# Revit family: 306_acb0105b96fc40aca24c2fe25a676a
name_source: partatom
category: Pipe Accessories
units: mm (PartAtom-declared; Revit-internal decimal feet)

## family parameters
Always vertical = Yes
Cut with Voids When Loaded = No
Part Type = Valve - Breaks Into
Round Connector Dimension = Use Diameter
Shared = No
Work Plane-Based = No

## types (4) — shared parameters
Description = 2-way Motorized ball valve MBA122, PN32 external thread with adapters
H1 = 1 mm  [stored 0.00328084 ft]
L2D_Min = 3048 mm
Manufacturer = ESBE
QmdConnectorList = 301;D;302;D
URL = http://www.esbe.eu
X15 = 8 mm  [stored 0.0262467 ft]
X15__ve = -8 mm  [stored -0.0262467 ft]
X16 = 6 mm  [stored 0.019685 ft]
X16__ve = -6 mm  [stored -0.019685 ft]
X8 = 4 mm  [stored 0.0131234 ft]
Y0 = 5 mm  [stored 0.0164042 ft]
Y11 = 3 mm  [stored 0.00984252 ft]
Z3 = 11 mm
Z4 = 52 mm
Z6 = 35 mm
Z6__ve = -35 mm
Z7 = 3 mm  [stored 0.00984252 ft]
magiPartTypeId = 306
magiProductFamilyId = acb0105b96fc40aca24c2fe25a676a

## per-type parameters (varying)
- MBA122 G1  MM WA 230VAC 2-P 10NM: C=73 mm; CenSd_Y13_6=14 mm  [stored 0.0459318 ft]; D=25 mm; E=29 mm; L2D=133 mm; W2D=25 mm; X1=75 mm; X12=58 mm; X12__ve=-58 mm; X14=4 mm  [stored 0.0131234 ft]; X17=47 mm; X5=3 mm  [stored 0.00984252 ft]; X5__ve=-3 mm; X6=33 mm; X7=20 mm  [stored 0.0656168 ft]; X7__ve=-20 mm; Y1=13 mm  [stored 0.0426509 ft]; Y10=19 mm; Y10__ve=-19 mm; Y12=15 mm  [stored 0.0492126 ft]; Y13=16 mm  [stored 0.0524934 ft]; Y14=14 mm  [stored 0.0459318 ft]; Y2=13 mm  [stored 0.0426509 ft]; Y4=15 mm  [stored 0.0492126 ft]; Y5=16 mm  [stored 0.0524934 ft]; Z2=26 mm; Z2__ve=-26 mm; Z5=3 mm  [stored 0.00984252 ft]; magiProductCode=MBA122 G1" MM WA 230VAC 2-P 10NM; magiProductId=a4835386385348b5886cc25a455dbb
- MBA122 G3/4  MM WA 230VAC 2-P 10NM: C=65 mm; CenSd_Y13_6=11 mm; D=20 mm; E=25 mm; L2D=50 mm; W2D=20 mm  [stored 0.0656168 ft]; X1=67 mm; X12=48 mm; X12__ve=-48 mm; X14=4 mm  [stored 0.0131234 ft]; X17=41 mm; X5=2 mm  [stored 0.00656168 ft]; X5__ve=-2 mm  [stored -0.00656168 ft]; X6=29 mm; X7=18 mm; X7__ve=-18 mm; Y1=10 mm  [stored 0.0328084 ft]; Y10=15 mm  [stored 0.0492126 ft]; Y10__ve=-15 mm; Y12=12 mm  [stored 0.0393701 ft]; Y13=13 mm  [stored 0.0426509 ft]; Y14=11 mm; Y2=10 mm  [stored 0.0328084 ft]; Y4=12 mm  [stored 0.0393701 ft]; Y5=12 mm  [stored 0.0393701 ft]; Z2=23 mm; Z2__ve=-23 mm; Z5=3 mm  [stored 0.00984252 ft]; magiProductCode=MBA122 G3/4" MM WA 230VAC 2-P 10NM; magiProductId=8c4dcbe5cc9140cea007b2309b293b
- MBA122 G1¼  MM WA 230VAC 2-P 10NM: C=74 mm; CenSd_Y13_6=18 mm; D=32 mm; E=34 mm; L2D=142 mm; W2D=32 mm; X1=79 mm; X12=64 mm; X12__ve=-64 mm; X14=4 mm  [stored 0.0131234 ft]; X17=50 mm; X5=3 mm  [stored 0.00984252 ft]; X5__ve=-3 mm; X6=36 mm; X7=21 mm; X7__ve=-21 mm; Y1=16 mm  [stored 0.0524934 ft]; Y10=24 mm; Y10__ve=-24 mm; Y12=19 mm; Y13=20 mm  [stored 0.0656168 ft]; Y14=18 mm; Y2=17 mm  [stored 0.0557743 ft]; Y4=19 mm; Y5=20 mm  [stored 0.0656168 ft]; Z2=31 mm; Z2__ve=-31 mm; Z5=3 mm  [stored 0.00984252 ft]; magiProductCode=MBA122 G1¼" MM WA 230VAC 2-P 10NM; magiProductId=521f458b085244f2b9d1e4ee08b93c
- MBA122 G1/2  MM WA 230VAC 2-P 10NM: C=59 mm; CenSd_Y13_6=8 mm  [stored 0.0262467 ft]; D=15 mm; E=22 mm; L2D=102 mm; W2D=15 mm  [stored 0.0492126 ft]; X1=59 mm; X12=38 mm; X12__ve=-38 mm; X14=3 mm  [stored 0.00984252 ft]; X17=36 mm; X5=2 mm  [stored 0.00656168 ft]; X5__ve=-2 mm  [stored -0.00656168 ft]; X6=26 mm; X7=15 mm  [stored 0.0492126 ft]; X7__ve=-15 mm; Y1=8 mm  [stored 0.0262467 ft]; Y10=11 mm; Y10__ve=-11 mm; Y12=9 mm  [stored 0.0295276 ft]; Y13=10 mm  [stored 0.0328084 ft]; Y14=8 mm  [stored 0.0262467 ft]; Y2=8 mm  [stored 0.0262467 ft]; Y4=9 mm  [stored 0.0295276 ft]; Y5=9 mm  [stored 0.0295276 ft]; Z2=19 mm; Z2__ve=-19 mm; Z5=2 mm  [stored 0.00656168 ft]; magiProductCode=MBA122 G1/2" MM WA 230VAC 2-P 10NM; magiProductId=d724465e1613473ca1039b751bb736

note: [stored X ft] marks values corroborated as IEEE doubles in the binary element streams (Revit-internal decimal feet)

## geometry (parser evidence)
native form markers: Sweep x2
no freeform markers — native parametric forms only
